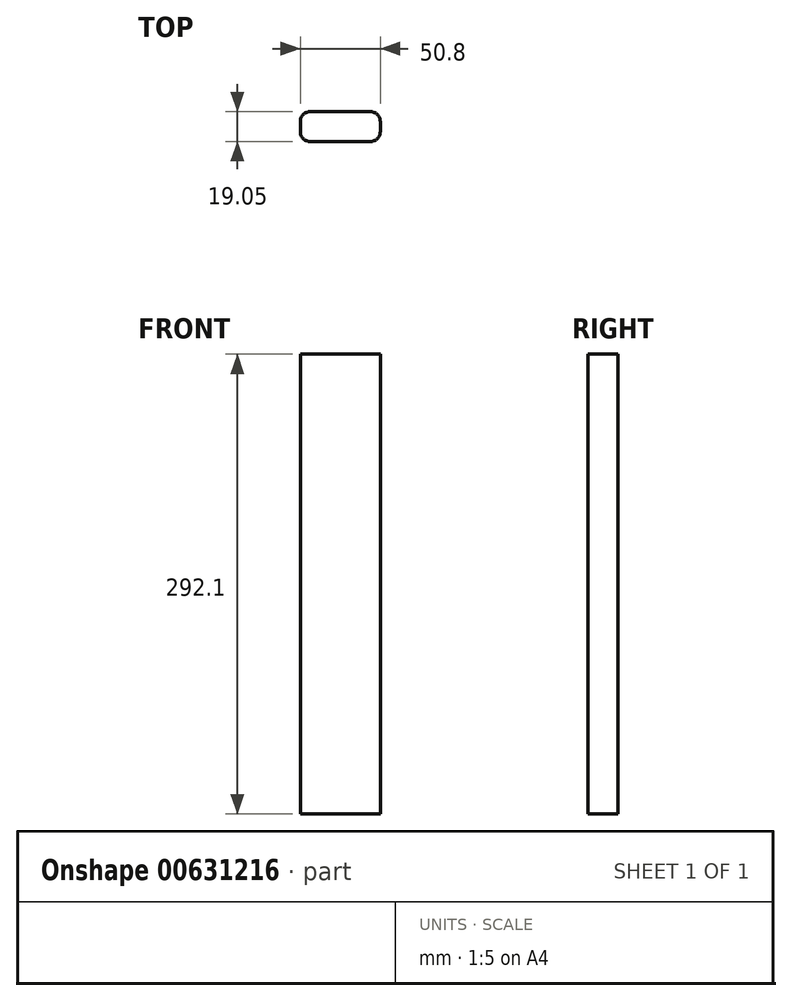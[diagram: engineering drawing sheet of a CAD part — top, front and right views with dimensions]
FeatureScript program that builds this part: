
annotation { "Feature Type Name" : "Feature", "Feature Type Description" : "" }
export const myFeature = defineFeature(function(context is Context, id is Id, definition is map)
    precondition{}
    {
        {
            var Q0;
            Q0=qCreatedBy(makeId("Front.planeOp"),FACE);
            var sketch = newSketch(context, id + "F0", { "sketchPlane" : qUnion([Q0])});
            skLineSegment(sketch, "E0.bottom", {"start": v(0, 0) * mm, "end": v(50.8, 0) * mm});
            skLineSegment(sketch, "E0.top", {"start": v(0, 292.1) * mm, "end": v(50.8, 292.1) * mm});
            skLineSegment(sketch, "E0.left", {"start": v(0, 0) * mm, "end": v(0, 292.1) * mm});
            skLineSegment(sketch, "E0.right", {"start": v(50.8, 0) * mm, "end": v(50.8, 292.1) * mm});
            skSolve(sketch);
        }
        {
            var Q0;
            Q0=makeQuery(id+"F0.imprint","IMPRINT",FACE,{"disambiguationData":[TD([[makeQuery(id+"F0.imprint","IMPRINT",EDGE,{"derivedFrom":sQuery(id+"F0.wireOp",EDGE,"E0.bottom")}),1.0]])]});
            extrude(context, id + "F1", {"entities" : qUnion([Q0]), "depth" : 19.05 * mm, "offsetDistance" : 25.4 * mm});
        }
        {
            var Q0;
            Q0=makeQuery(id+"F1.opExtrude","CAP_EDGE",EDGE,{"disambiguationData":[OSD([sQuery(id+"F0.wireOp",EDGE,"E0.right")])],"isStart":false});
            var Q1;
            Q1=makeQuery(id+"F1.opExtrude","CAP_EDGE",EDGE,{"disambiguationData":[OSD([sQuery(id+"F0.wireOp",EDGE,"E0.right")])],"isStart":true});
            var Q2;
            Q2=makeQuery(id+"F1.opExtrude","CAP_EDGE",EDGE,{"disambiguationData":[OSD([sQuery(id+"F0.wireOp",EDGE,"E0.left")])],"isStart":false});
            var Q3;
            Q3=makeQuery(id+"F1.opExtrude","CAP_EDGE",EDGE,{"disambiguationData":[OSD([sQuery(id+"F0.wireOp",EDGE,"E0.left")])],"isStart":true});
            fillet(context, id + "F2", {"entities" : qUnion([Q0, Q1, Q2, Q3]), "radius" : 6.35 * mm, "tangentPropagation" : true, "allowEdgeOverflow" : false});
        }
    });
